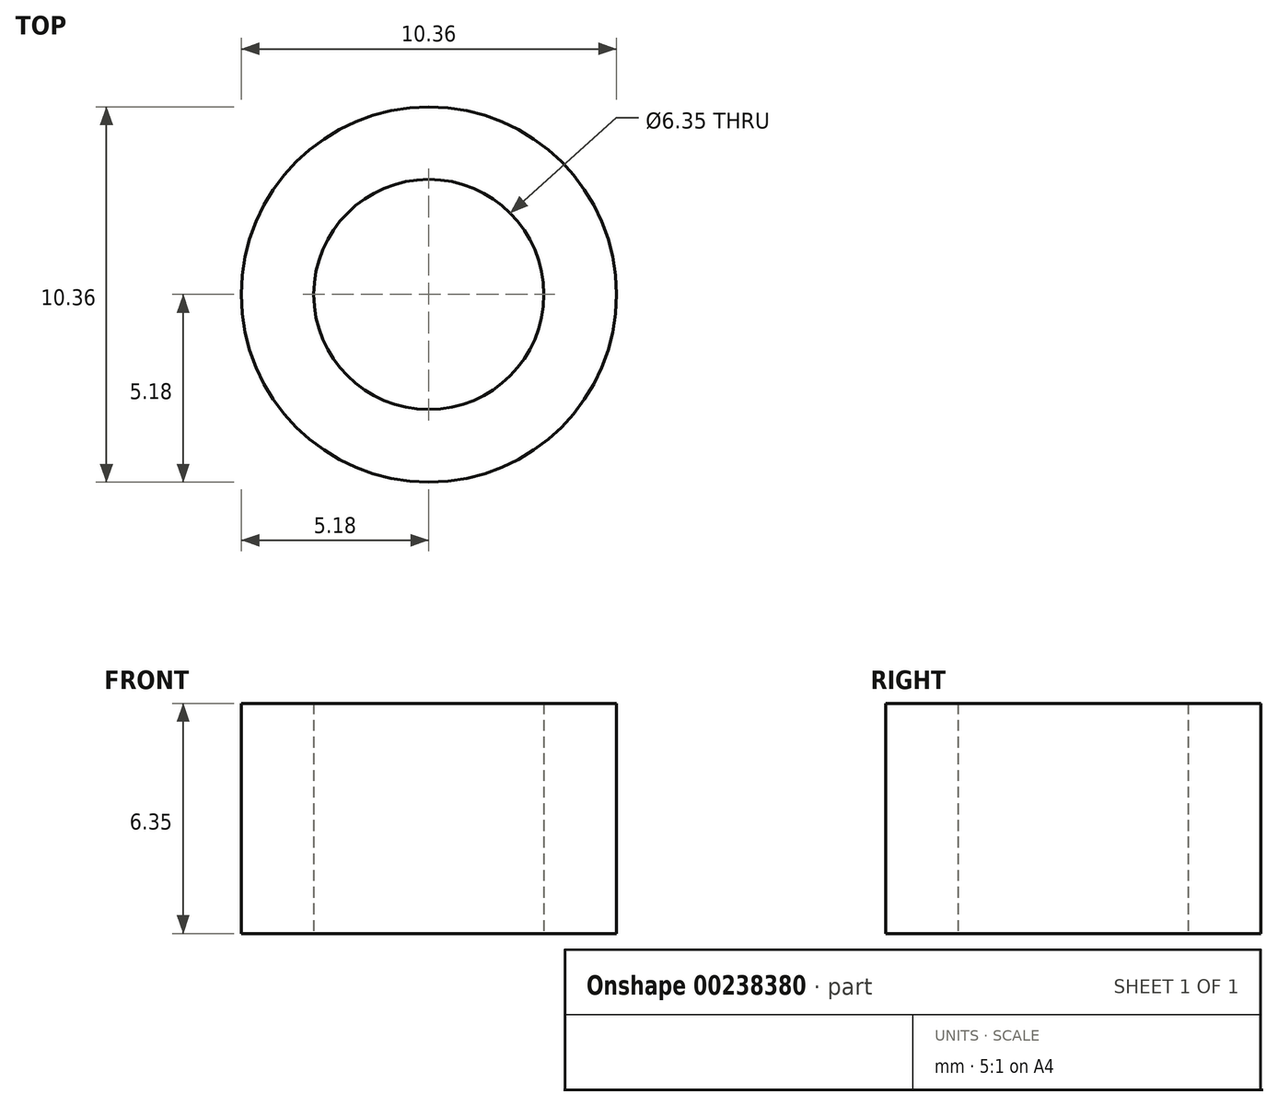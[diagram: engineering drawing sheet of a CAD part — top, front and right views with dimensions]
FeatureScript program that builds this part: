
annotation { "Feature Type Name" : "Feature", "Feature Type Description" : "" }
export const myFeature = defineFeature(function(context is Context, id is Id, definition is map)
    precondition{}
    {
        {
            var Q0;
            Q0=qCreatedBy(makeId("Top.planeOp"),FACE);
            var sketch = newSketch(context, id + "F0", { "sketchPlane" : qUnion([Q0])});
            skCircle(sketch, "E0", {"center": v(0, 0) * mm, "radius": 3.18 * mm});
            skCircle(sketch, "E1.0", {"center": v(0, 0) * mm, "radius": 5.18 * mm});
            skSolve(sketch);
        }
        {
            var Q0;
            Q0=makeQuery(id+"F0.imprint","IMPRINT",FACE,{"disambiguationData":[TD([[makeQuery(id+"F0.imprint","IMPRINT",EDGE,{"derivedFrom":sQuery(id+"F0.wireOp",EDGE,"E0")}),-1.0]])]});
            extrude(context, id + "F1", {"entities" : qUnion([Q0]), "depth" : 6.35 * mm});
        }
    });
